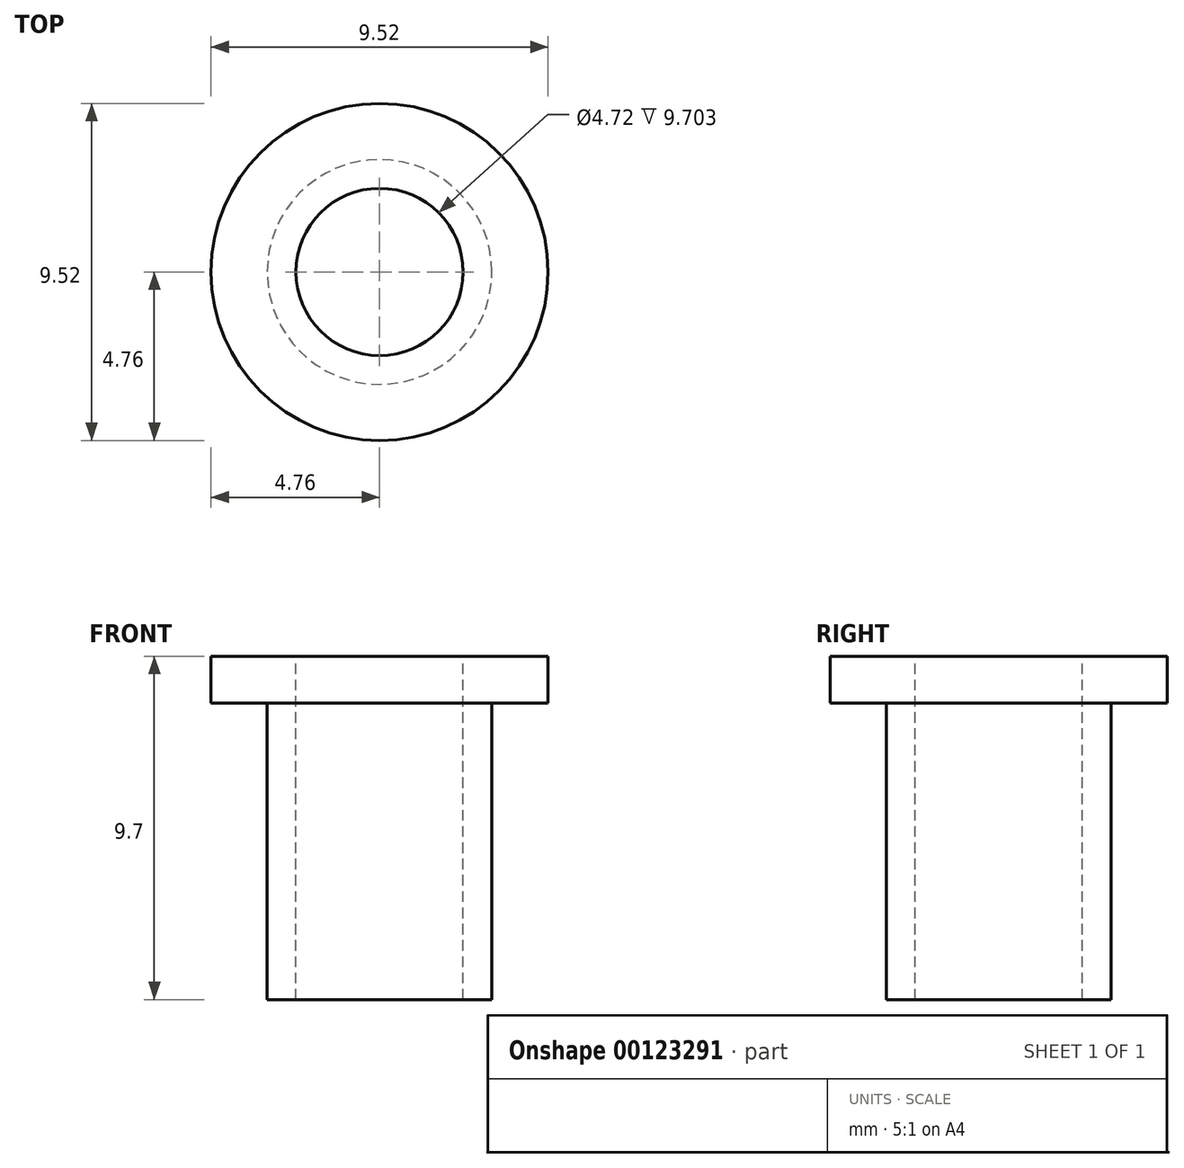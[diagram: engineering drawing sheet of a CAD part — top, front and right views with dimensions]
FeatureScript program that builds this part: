
annotation { "Feature Type Name" : "Feature", "Feature Type Description" : "" }
export const myFeature = defineFeature(function(context is Context, id is Id, definition is map)
    precondition{}
    {
        {
            var Q0;
            Q0=qCreatedBy(makeId("Top.planeOp"),FACE);
            var sketch = newSketch(context, id + "F0", { "sketchPlane" : qUnion([Q0])});
            skCircle(sketch, "E0", {"center": v(0, 0) * mm, "radius": 4.76 * mm});
            skSolve(sketch);
        }
        {
            var Q0;
            Q0 = qSketchRegion(id + "F0", true);
            extrude(context, id + "F1", {"entities" : qUnion([Q0]), "depth" : 9.7 * mm});
        }
        {
            var Q0;
            Q0=makeQuery(id+"F1.opExtrude","CAP_FACE",FACE,{"disambiguationData":[OSD([sQuery(id+"F0.wireOp",EDGE,"E0")])],"isStart":false});
            var sketch = newSketch(context, id + "F2", { "sketchPlane" : qUnion([Q0])});
            skCircle(sketch, "E1", {"center": v(0, 0) * mm, "radius": 2.36 * mm});
            skSolve(sketch);
        }
        {
            var Q0;
            Q0 = qSketchRegion(id + "F2", true);
            extrude(context, id + "F3", {"entities" : qUnion([Q0]), "operationType" : NewBodyOperationType.REMOVE, "endBound" : BoundingType.UP_TO_NEXT, "oppositeDirection" : true, "depth" : 25.4 * mm});
        }
        {
            var Q0;
            Q0=makeQuery(id+"F1.opExtrude","CAP_FACE",FACE,{"disambiguationData":[OSD([sQuery(id+"F0.wireOp",EDGE,"E0")])],"isStart":true});
            var sketch = newSketch(context, id + "F4", { "sketchPlane" : qUnion([Q0])});
            skCircle(sketch, "E2", {"center": v(0, 0) * mm, "radius": 3.17 * mm});
            skSolve(sketch);
        }
        {
            var Q0;
            Q0=makeQuery(id+"F4.imprint","IMPRINT",FACE,{"disambiguationData":[TD([[makeQuery(id+"F4.imprint","IMPRINT",EDGE,{"derivedFrom":sQuery(id+"F4.wireOp",EDGE,"E2")}),-1.0]])]});
            extrude(context, id + "F5", {"entities" : qUnion([Q0]), "operationType" : NewBodyOperationType.REMOVE, "oppositeDirection" : true, "depth" : 8.38 * mm});
        }
    });
